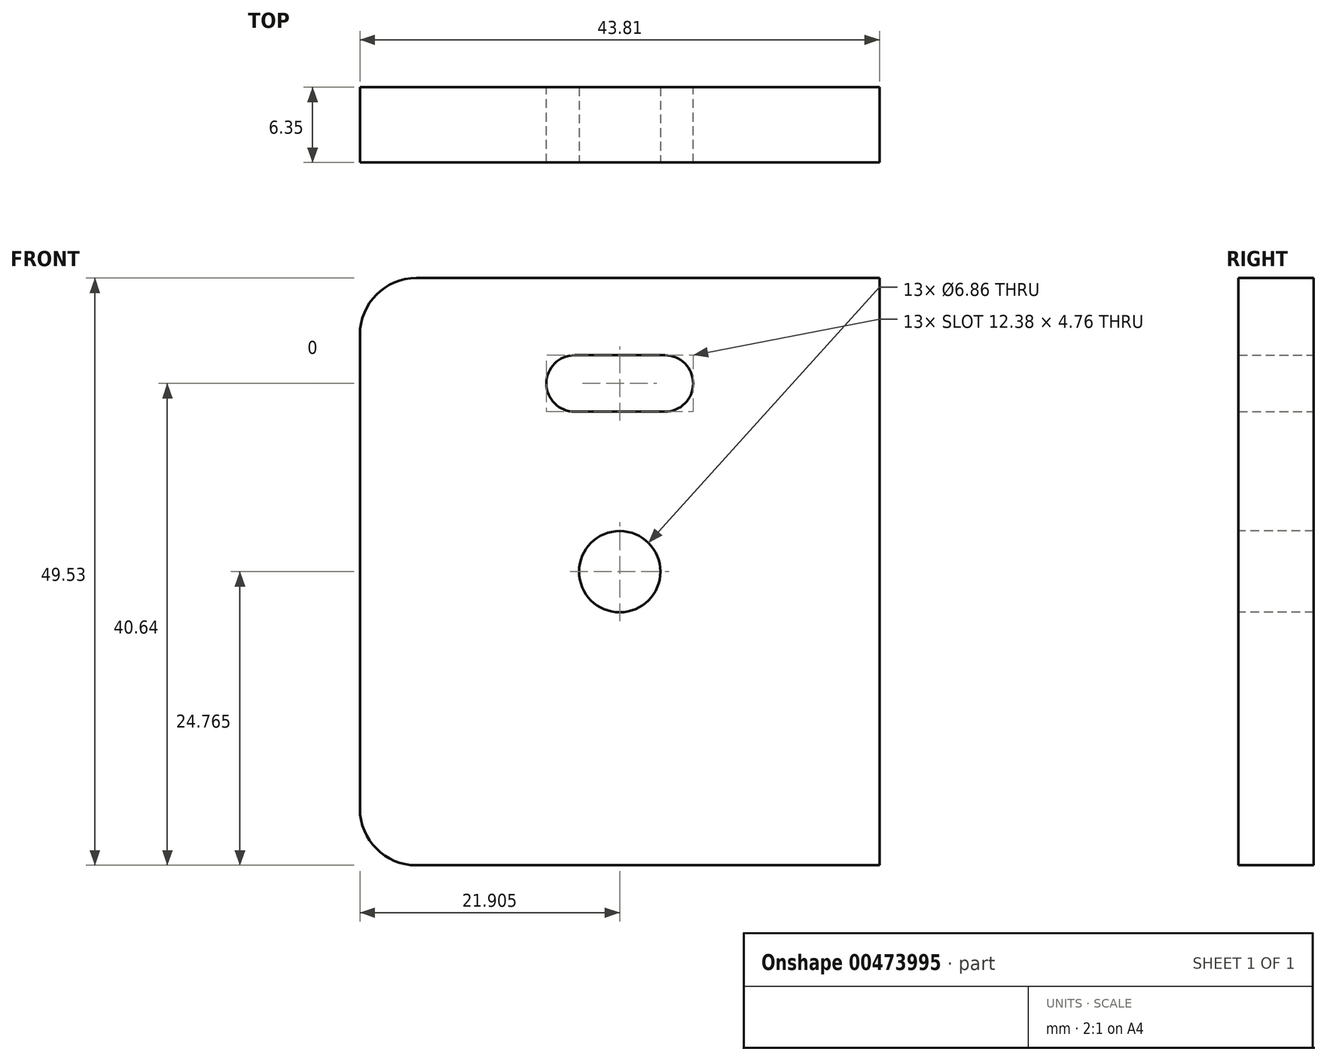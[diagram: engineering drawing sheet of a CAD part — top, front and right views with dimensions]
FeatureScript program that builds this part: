
annotation { "Feature Type Name" : "Feature", "Feature Type Description" : "" }
export const myFeature = defineFeature(function(context is Context, id is Id, definition is map)
    precondition{}
    {
        {
            var Q0;
            Q0=qCreatedBy(makeId("Front.planeOp"),FACE);
            var sketch = newSketch(context, id + "F0", { "sketchPlane" : qUnion([Q0])});
            skLineSegment(sketch, "E0.0", {"start": v(-4.76, 44.77) * mm, "end": v(-4.76, 4.76) * mm});
            skArc(sketch, "E1.0", {"start": v(0, 0) * mm, "mid": v(-3.37, 1.4) * mm, "end": v(-4.76, 4.76) * mm});
            skLineSegment(sketch, "E1.1", {"start": v(0, 49.53) * mm, "end": v(39.05, 49.53) * mm});
            skArc(sketch, "E1.2", {"start": v(-4.76, 44.77) * mm, "mid": v(-3.37, 48.14) * mm, "end": v(0, 49.53) * mm});
            skLineSegment(sketch, "E1.3", {"start": v(0, 0) * mm, "end": v(39.05, 0) * mm});
            skLineSegment(sketch, "E1.4", {"start": v(39.05, 14.29) * mm, "end": v(39.05, 35.24) * mm});
            skLineSegment(sketch, "E1.5", {"start": v(39.05, 46.35) * mm, "end": v(39.05, 35.24) * mm});
            skLineSegment(sketch, "E1.6", {"start": v(39.05, 46.35) * mm, "end": v(39.05, 49.53) * mm});
            skLineSegment(sketch, "E1.7", {"start": v(39.05, 0) * mm, "end": v(39.05, 3.18) * mm});
            skLineSegment(sketch, "E2", {"start": v(39.05, 14.29) * mm, "end": v(39.05, 3.18) * mm});
            skSolve(sketch);
        }
        {
            var Q0;
            Q0=makeQuery(id+"F0.imprint","IMPRINT",FACE,{"disambiguationData":[TD([[makeQuery(id+"F0.imprint","IMPRINT",EDGE,{"derivedFrom":sQuery(id+"F0.wireOp",EDGE,"E0.0")}),1.0]])]});
            extrude(context, id + "F1", {"entities" : qUnion([Q0]), "depth" : 6.35 * mm});
        }
        {
            var Q0;
            Q0=makeQuery(id+"F1.opExtrude","CAP_FACE",FACE,{"disambiguationData":[OSD([sQuery(id+"F0.wireOp",EDGE,"E0.0"),sQuery(id+"F0.wireOp",EDGE,"E1.0"),sQuery(id+"F0.wireOp",EDGE,"E1.1"),sQuery(id+"F0.wireOp",EDGE,"E1.2"),sQuery(id+"F0.wireOp",EDGE,"E1.3"),sQuery(id+"F0.wireOp",EDGE,"E1.4"),sQuery(id+"F0.wireOp",EDGE,"E1.5"),sQuery(id+"F0.wireOp",EDGE,"E1.6"),sQuery(id+"F0.wireOp",EDGE,"E1.7"),sQuery(id+"F0.wireOp",EDGE,"E2")])],"isStart":false});
            var sketch = newSketch(context, id + "F2", { "sketchPlane" : qUnion([Q0])});
            skPoint(sketch, "E3", {"position": v(17.14, 24.77) * mm});
            skLineSegment(sketch, "E4.0.0", {"start": v(39.05, 0) * mm, "end": v(39.05, 49.53) * mm});
            skLineSegment(sketch, "E4.0.1", {"start": v(39.05, 49.53) * mm, "end": v(0, 49.53) * mm});
            skArc(sketch, "E4.0.2", {"start": v(0, 49.53) * mm, "mid": v(-3.37, 48.14) * mm, "end": v(-4.76, 44.77) * mm});
            skLineSegment(sketch, "E4.0.3", {"start": v(-4.76, 44.77) * mm, "end": v(-4.76, 4.76) * mm});
            skArc(sketch, "E4.0.4", {"start": v(-4.76, 4.76) * mm, "mid": v(-3.37, 1.4) * mm, "end": v(0, 0) * mm});
            skLineSegment(sketch, "E4.0.5", {"start": v(0, 0) * mm, "end": v(39.05, 0) * mm});
            skSolve(sketch);
        }
        {
            var Q0;
            Q0=sQuery(id+"F2.wireOp",VERTEX,"E3");
            var Q1;
            Q1=makeQuery(id+"F1.opExtrude","SWEPT_BODY",BODY,{"disambiguationData":[OSD([sQuery(id+"F0.wireOp",EDGE,"E0.0"),sQuery(id+"F0.wireOp",EDGE,"E1.0"),sQuery(id+"F0.wireOp",EDGE,"E1.1"),sQuery(id+"F0.wireOp",EDGE,"E1.2"),sQuery(id+"F0.wireOp",EDGE,"E1.3"),sQuery(id+"F0.wireOp",EDGE,"E1.4"),sQuery(id+"F0.wireOp",EDGE,"E1.5"),sQuery(id+"F0.wireOp",EDGE,"E1.6"),sQuery(id+"F0.wireOp",EDGE,"E1.7"),sQuery(id+"F0.wireOp",EDGE,"E2")])]});
            hole(context, id + "F3", {"style" : HoleStyle.SIMPLE, "endStyle" : HoleEndStyle.BLIND, "holeDiameter" : 6.86 * mm, "holeDepth" : 12.7 * mm, "isTappedThrough" : true, "tappedDepth" : 3.96 * mm, "tapClearance" : 3, "locations" : qUnion([Q0]), "scope" : qUnion([Q1])});
        }
        {
            var Q0;
            Q0=makeQuery(id+"F1.opExtrude","CAP_FACE",FACE,{"disambiguationData":[OSD([sQuery(id+"F0.wireOp",EDGE,"E0.0"),sQuery(id+"F0.wireOp",EDGE,"E1.0"),sQuery(id+"F0.wireOp",EDGE,"E1.1"),sQuery(id+"F0.wireOp",EDGE,"E1.2"),sQuery(id+"F0.wireOp",EDGE,"E1.3"),sQuery(id+"F0.wireOp",EDGE,"E1.4"),sQuery(id+"F0.wireOp",EDGE,"E1.5"),sQuery(id+"F0.wireOp",EDGE,"E1.6"),sQuery(id+"F0.wireOp",EDGE,"E1.7"),sQuery(id+"F0.wireOp",EDGE,"E2")])],"isStart":true});
            var sketch = newSketch(context, id + "F4", { "sketchPlane" : qUnion([Q0])});
            skLineSegment(sketch, "E5.0.0", {"start": v(-39.05, 49.53) * mm, "end": v(-39.05, 0) * mm});
            skLineSegment(sketch, "E5.0.1", {"start": v(-39.05, 0) * mm, "end": v(0, 0) * mm});
            skArc(sketch, "E5.0.2", {"start": v(0, 0) * mm, "mid": v(3.37, 1.4) * mm, "end": v(4.76, 4.76) * mm});
            skLineSegment(sketch, "E5.0.3", {"start": v(4.76, 4.76) * mm, "end": v(4.76, 44.77) * mm});
            skArc(sketch, "E5.0.4", {"start": v(4.76, 44.77) * mm, "mid": v(3.37, 48.14) * mm, "end": v(0, 49.53) * mm});
            skLineSegment(sketch, "E5.0.5", {"start": v(0, 49.53) * mm, "end": v(-39.05, 49.53) * mm});
            skCircle(sketch, "E6", {"center": v(-20.96, 40.64) * mm, "radius": 2.38 * mm});
            skCircle(sketch, "E7", {"center": v(-13.34, 40.64) * mm, "radius": 2.38 * mm});
            skLineSegment(sketch, "E8", {"start": v(-20.96, 43.02) * mm, "end": v(-13.34, 43.02) * mm});
            skLineSegment(sketch, "E9", {"start": v(-20.96, 38.26) * mm, "end": v(-13.34, 38.26) * mm});
            skPoint(sketch, "E10", {"position": v(-17.14, 40.64) * mm});
            skSolve(sketch);
        }
        {
            var Q0;
            {var subQ0=sQuery(id+"F4.wireOp",EDGE,"E8");Q0=makeQuery(id+"F4.imprint","IMPRINT",FACE,{"disambiguationData":[TD([[makeQuery(id+"F4.imprint","IMPRINT",EDGE,{"derivedFrom":subQ0}),-1.0]])]});}
            var Q1;
            {var subQ0=sQuery(id+"F4.wireOp",EDGE,"E6");var subQ1=makeQuery(id+"F4.imprint","INTERSECT",VERTEX,{"derivedFrom":[subQ0,sQuery(id+"F4.wireOp",EDGE,"E8")]});Q1=makeQuery(id+"F4.imprint","IMPRINT",FACE,{"disambiguationData":[TD([[makeQuery(id+"F4.imprint","IMPRINT",EDGE,{"disambiguationData":[TD([[subQ1,-1.0]])],"derivedFrom":subQ0}),1.0]])]});}
            var Q2;
            {var subQ0=sQuery(id+"F4.wireOp",EDGE,"E7");var subQ1=makeQuery(id+"F4.imprint","INTERSECT",VERTEX,{"derivedFrom":[subQ0,sQuery(id+"F4.wireOp",EDGE,"E8")]});Q2=makeQuery(id+"F4.imprint","IMPRINT",FACE,{"disambiguationData":[TD([[makeQuery(id+"F4.imprint","IMPRINT",EDGE,{"disambiguationData":[TD([[subQ1,-1.0]])],"derivedFrom":subQ0}),1.0]])]});}
            extrude(context, id + "F5", {"entities" : qUnion([Q0, Q1, Q2]), "operationType" : NewBodyOperationType.REMOVE, "oppositeDirection" : true, "depth" : 25.4 * mm});
        }
    });
